# Revit family: Faucet-Kitchen_Sink-KOHLER-Forte-K-10443
name_source: partatom
category: Plumbing Fixtures
revit_build: Autodesk Revit 2015 (Build: 20140606_1530(x64)
units: mm (PartAtom-declared; Revit-internal decimal feet)

## types (3) — shared parameters
ADA Compliant = Yes
Assembly Code = D2010900
CW Connection = Yes
Date Modified = 09/17/2017
Default Elevation = 32"
Description = Two-hole bar sink faucet with lever handle
Flow Rate = 2 GPM
HW Connection = Yes
Height = 10 3/32"
Length = 9 17/32"
Manufacturer = Kohler
MasterFormat 1995 = 15410
MasterFormat 2004 = 22.41.39
Material = Premium metal construction
Pressure = 60.00 psi
Product Documentation Link = http://www.us.kohler.com
Product Name = Forté
Product Page URL = http://www.us.kohler.com
URL = http://www.us.kohler.com
Width = 5 29/32"

## per-type parameters (varying)
| type | Finish | Model | Type |
| CP-Polished Chrome | Metal-Kohler-CP-Polished Chrome | K-10443-CP | 1 |
| BN-Vibrant Brushed Nickel | Metal-Kohler-BN-Vibrant Brushed Nickel | K-10443-BN | 2 |
| VS-Vibrant Stainless | Metal-Kohler-VS-Vibrant Stainless | K-10443-VS | 3 |

## geometry (parser evidence)
native form markers: Sweep x5
no freeform markers — native parametric forms only
